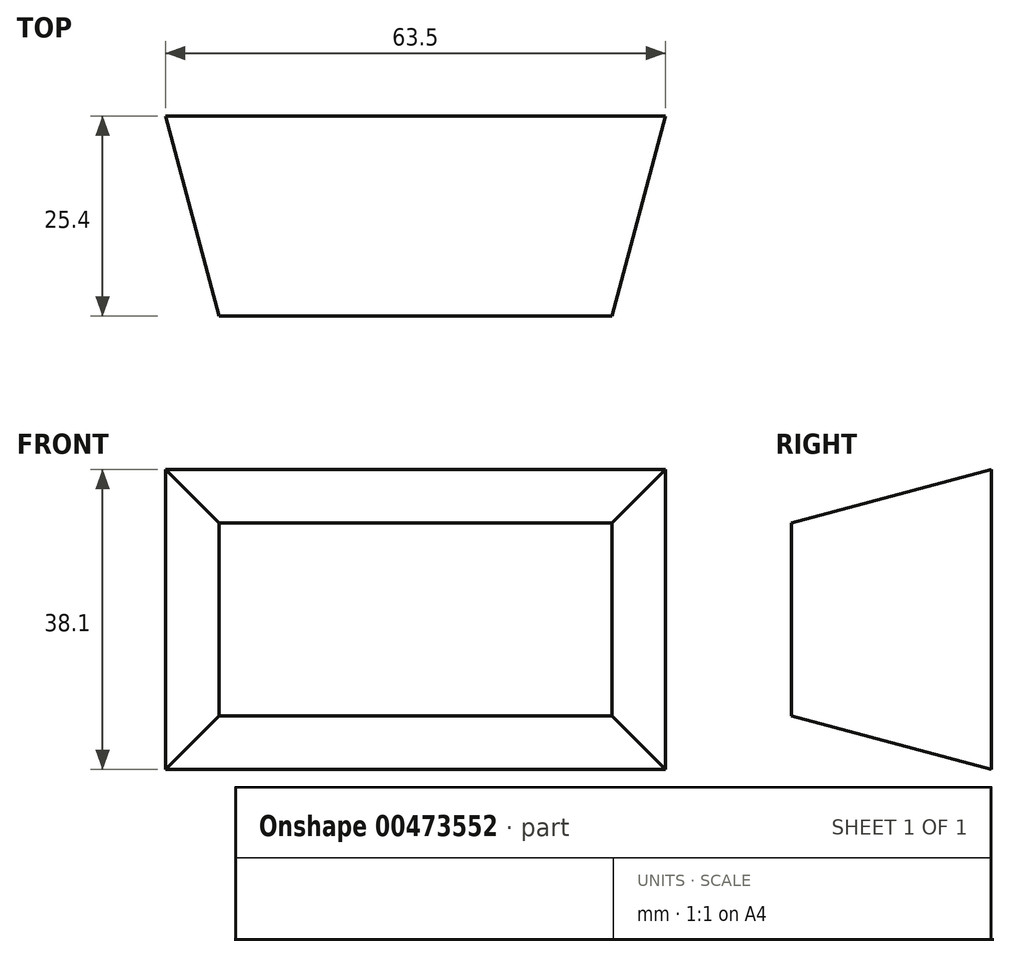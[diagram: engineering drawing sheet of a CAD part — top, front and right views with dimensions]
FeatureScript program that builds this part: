
annotation { "Feature Type Name" : "Feature", "Feature Type Description" : "" }
export const myFeature = defineFeature(function(context is Context, id is Id, definition is map)
    precondition{}
    {
        {
            var Q0;
            Q0=qCreatedBy(makeId("Front.planeOp"),FACE);
            var sketch = newSketch(context, id + "F0", { "sketchPlane" : qUnion([Q0])});
            skLineSegment(sketch, "E0.bottom", {"start": v(-63.5, 19.05) * mm, "end": v(0, 19.05) * mm});
            skLineSegment(sketch, "E0.top", {"start": v(-63.5, -19.05) * mm, "end": v(0, -19.05) * mm});
            skLineSegment(sketch, "E0.left", {"start": v(-63.5, 19.05) * mm, "end": v(-63.5, -19.05) * mm});
            skLineSegment(sketch, "E0.right", {"start": v(0, 19.05) * mm, "end": v(0, -19.05) * mm});
            skSolve(sketch);
        }
        {
            var Q0;
            Q0 = qSketchRegion(id + "F0", true);
            extrude(context, id + "F1", {"entities" : qUnion([Q0]), "depth" : 25.4 * mm, "hasDraft" : true, "draftAngle" : 15 * degree, "draftPullDirection" : true});
        }
    });
